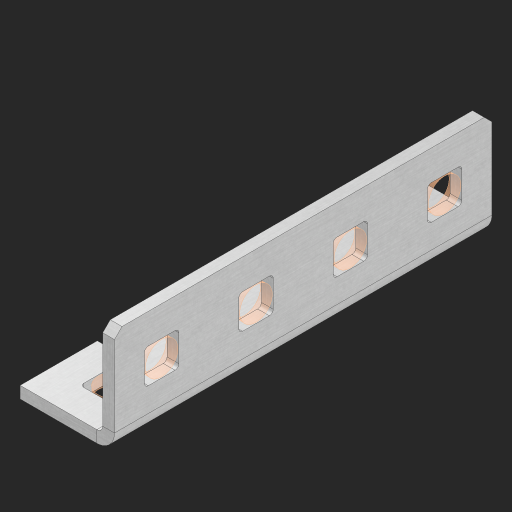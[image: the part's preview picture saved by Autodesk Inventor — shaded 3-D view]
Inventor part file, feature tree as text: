
AUTODESK INVENTOR PART (.ipt)
format: ipt  version: 2023 (Build 270158000, 158)  size: 570,880 bytes
history: native  units: in
note: dims shown in document units (in); Inventor stores cm internally (conversion verified against a paired STEP export)
features: other x160, sheet_metal_op x11, extrude x10, sketch x10, pattern_linear x2, mirror x1, chamfer x1
ambient origin geometry x8: Origin, YZ Plane, XZ Plane, XY Plane, X Axis, Y Axis, Z Axis, Center Point
bodies: Solid1 (feature_tree), Body (feature_tree)
feature tree (195):
  other  "Alu Half C 1x2x1x4"
  other  "Table"
  other  "Alu C 1x2x1x35"
  other  "Alu C 1x2x1x34"
  other  "Alu C 1x2x1x33"
  other  "Alu C 1x2x1x32"
  other  "Alu C 1x2x1x31"
  other  "Alu C 1x2x1x30"
  other  "Alu C 1x2x1x29"
  other  "Alu C 1x2x1x28"
  other  "Alu C 1x2x1x27"
  other  "Alu C 1x2x1x26"
  other  "Alu C 1x2x1x25"
  other  "Alu C 1x2x1x24"
  other  "Alu C 1x2x1x23"
  other  "Alu C 1x2x1x22"
  other  "Alu C 1x2x1x21"
  other  "Alu C 1x2x1x20"
  other  "Alu C 1x2x1x19"
  other  "Alu C 1x2x1x18"
  other  "Alu C 1x2x1x17"
  other  "Alu C 1x2x1x16"
  other  "Alu C 1x2x1x15"
  other  "Alu C 1x2x1x14"
  other  "Alu C 1x2x1x13"
  other  "Alu C 1x2x1x12"
  other  "Alu C 1x2x1x11"
  other  "Alu C 1x2x1x10"
  other  "Alu C 1x2x1x9"
  other  "Alu C 1x2x1x8"
  other  "Alu C 1x2x1x7"
  other  "Alu C 1x2x1x6"
  other  "Alu C 1x2x1x5"
  other  "Alu C 1x2x1x4"
  other  "Alu C 1x2x1x3"
  other  "Alu C 1x2x1x2"
  other  "Alu C 1x2x1x1"
  other  "Steel C 1x2x1x35"
  other  "Steel C 1x2x1x34"
  other  "Steel C 1x2x1x33"
  other  "Steel C 1x2x1x32"
  other  "Steel C 1x2x1x31"
  other  "Steel C 1x2x1x30"
  other  "Steel C 1x2x1x29"
  other  "Steel C 1x2x1x28"
  other  "Steel C 1x2x1x27"
  other  "Steel C 1x2x1x26"
  other  "Steel C 1x2x1x25"
  other  "Steel C 1x2x1x24"
  other  "Steel C 1x2x1x23"
  other  "Steel C 1x2x1x22"
  other  "Steel C 1x2x1x21"
  other  "Steel C 1x2x1x20"
  other  "Steel C 1x2x1x19"
  other  "Steel C 1x2x1x18"
  other  "Steel C 1x2x1x17"
  other  "Steel C 1x2x1x16"
  other  "Steel C 1x2x1x15"
  other  "Steel C 1x2x1x14"
  other  "Steel C 1x2x1x13"
  other  "Steel C 1x2x1x12"
  other  "Steel C 1x2x1x11"
  other  "Steel C 1x2x1x10"
  other  "Steel C 1x2x1x9"
  other  "Steel C 1x2x1x8"
  other  "Steel C 1x2x1x7"
  other  "Steel C 1x2x1x6"
  other  "Steel C 1x2x1x5"
  other  "Steel C 1x2x1x4"
  other  "Steel C 1x2x1x3"
  other  "Steel C 1x2x1x2"
  other  "Steel C 1x2x1x1"
  other  "Alu Half C 1x2x1x35"
  other  "Alu Half C 1x2x1x34"
  other  "Alu Half C 1x2x1x33"
  other  "Alu Half C 1x2x1x32"
  other  "Alu Half C 1x2x1x31"
  other  "Alu Half C 1x2x1x30"
  other  "Alu Half C 1x2x1x29"
  other  "Alu Half C 1x2x1x28"
  other  "Alu Half C 1x2x1x27"
  other  "Alu Half C 1x2x1x26"
  other  "Alu Half C 1x2x1x25"
  other  "Alu Half C 1x2x1x24"
  other  "Alu Half C 1x2x1x23"
  other  "Alu Half C 1x2x1x22"
  other  "Alu Half C 1x2x1x21"
  other  "Alu Half C 1x2x1x20"
  other  "Alu Half C 1x2x1x19"
  other  "Alu Half C 1x2x1x18"
  other  "Alu Half C 1x2x1x17"
  other  "Alu Half C 1x2x1x16"
  other  "Alu Half C 1x2x1x15"
  other  "Alu Half C 1x2x1x14"
  other  "Alu Half C 1x2x1x13"
  other  "Alu Half C 1x2x1x12"
  other  "Alu Half C 1x2x1x11"
  other  "Alu Half C 1x2x1x10"
  other  "Alu Half C 1x2x1x9"
  other  "Alu Half C 1x2x1x8"
  other  "Alu Half C 1x2x1x7"
  other  "Alu Half C 1x2x1x6"
  other  "Alu Half C 1x2x1x5"
  other  "Alu Half C 1x2x1x3"
  other  "Alu Half C 1x2x1x2"
  other  "Alu Half C 1x2x1x1"
  other  "Steel Half C 1x2x1x35"
  other  "Steel Half C 1x2x1x34"
  other  "Steel Half C 1x2x1x33"
  other  "Steel Half C 1x2x1x32"
  other  "Steel Half C 1x2x1x31"
  other  "Steel Half C 1x2x1x30"
  other  "Steel Half C 1x2x1x29"
  other  "Steel Half C 1x2x1x28"
  other  "Steel Half C 1x2x1x27"
  other  "Steel Half C 1x2x1x26"
  other  "Steel Half C 1x2x1x25"
  other  "Steel Half C 1x2x1x24"
  other  "Steel Half C 1x2x1x23"
  other  "Steel Half C 1x2x1x22"
  other  "Steel Half C 1x2x1x21"
  other  "Steel Half C 1x2x1x20"
  other  "Steel Half C 1x2x1x19"
  other  "Steel Half C 1x2x1x18"
  other  "Steel Half C 1x2x1x17"
  other  "Steel Half C 1x2x1x16"
  other  "Steel Half C 1x2x1x15"
  other  "Steel Half C 1x2x1x14"
  other  "Steel Half C 1x2x1x13"
  other  "Steel Half C 1x2x1x12"
  other  "Steel Half C 1x2x1x11"
  other  "Steel Half C 1x2x1x10"
  other  "Steel Half C 1x2x1x9"
  other  "Steel Half C 1x2x1x8"
  other  "Steel Half C 1x2x1x7"
  other  "Steel Half C 1x2x1x6"
  other  "Steel Half C 1x2x1x5"
  other  "Steel Half C 1x2x1x4"
  other  "Steel Half C 1x2x1x3"
  other  "Steel Half C 1x2x1x2"
  other  "Steel Half C 1x2x1x1"
  sheet_metal_op  "Flanges"
  other  "Flange Pattern Plane"
  other  "Flange Pattern Sketch"
  sheet_metal_op  "Flange Pattern"
  sheet_metal_op  "Body Pattern"
  pattern_linear  "Center Pattern"  Spacing1=0.0625in  [1 undecoded]
  other  "Arc Length"
  mirror  "Notch Mirror"
  pattern_linear  "Notch Pattern"  Spacing1=0.182in  [1 undecoded]
  chamfer  "End Chamfer"
  extrude  "Half Cut"  Depth=0.02in
  sketch  "Sketch1"  dims[d0=1.0in]
  other  "Plate1"
  sketch  "Sketch2"  dims[d1=2.0in]
  other  "Plate2"
  sheet_metal_op  "Bend1"
  sheet_metal_op  "Corner1"
  sketch  "Sketch3"  dims[d2=0.0625in]
  sketch  "Sketch7"  dims[d3=0.0625in]
  other  "Srf1"
  other  "Srf2"
  sketch  "Sketch8"  dims[d4=0.0312in]
  sketch  "Sketch9"  dims[d5=0.125in]
  other  "Srf91"
  sheet_metal_op  "Body Pattern Sketch"
  other  "Srf92"
  sketch  "Sketch13"  dims[d6=0.0625in]
  sketch  "Sketch14"  dims[d7=0.5in d8=90.0deg d9=0.0312in]
  sketch  "Sketch15"  dims[d10=0.25in]
  sketch  "Sketch16"  dims[d11=0.0625in d12=0.0625in d16=0.182in d17=0.02in d18=0.0625in d19=0.0in d20=0.25in d21=0.25in d38=1.5748in d40=0.5in d41=0.3937in d43=1.0in d46=0.172in d47=1.0in d48=0.0in d49=0.182in d50=0.02in d51=0.25in d52=0.25in d53=0.0625in d54=0.0in d55=0.172in d56=1.0in d57=0.0in d58=0.25in d60=1.5748in d62=0.5in d63=0.3937in d65=0.5in d85=0.1473in d86=0.1782in d88=0.04in d89=0.0625in d90=0.0in d91=0.04in d92=0.0491in d95=2.5in d96=0.04in d97=0.25in d98=45.0deg d99=0.25in d100=0.5in d101=0.0in d102=2.497in d106=0.182in d107=0.02in d108=0.5in d109=0.5in d110=0.0625in d111=0.0in d112=0.172in d113=0.5in d114=0.0in d117=0.5in d118=0.5in d119=0.5in]
  other  "Srf786"
  other  "Srf823"
  other  "Srf824"
  other  "Srf856"
  other  "Srf857"
  other  "Srf889"
  other  "Srf890"
  other  "Srf891"
  sheet_metal_op  "Flange Stamp"
  sheet_metal_op  "Flange Circle"
  sheet_metal_op  "Body Stamp"
  sheet_metal_op  "Body Circle"
  other  "Center Stamp"
  other  "Center Circle"
  sheet_metal_op  "Notch"
  extrude  "ExtrusionSrf2"  Depth=0.0625in
  extrude  "ExtrusionSrf92"  TaperAngle=0.0deg  [1 undecoded]
  extrude  "ExtrusionSrf823"  Depth=0.25in
  extrude  "ExtrusionSrf824"  Depth=0.25in
  extrude  "ExtrusionSrf856"  Depth=0.5in
  extrude  "ExtrusionSrf857"  Depth=0.5in
  extrude  "ExtrusionSrf889"  Depth=1.0in TaperAngle=0.0deg
  extrude  "ExtrusionSrf890"  Depth=0.182in
  extrude  "ExtrusionSrf891"  Depth=0.02in
note: 3 required parameter values undecoded (feature->parameter linkage not recoverable at this tier; creation-order binding heuristic only, values carry confidence <= 0.55)
